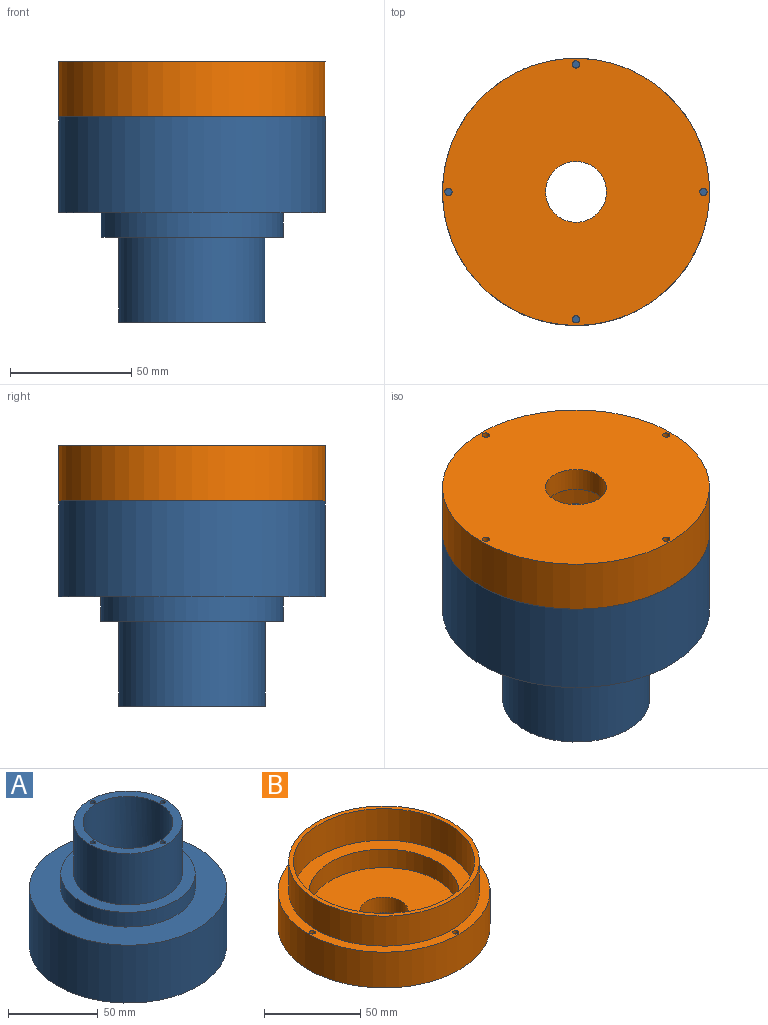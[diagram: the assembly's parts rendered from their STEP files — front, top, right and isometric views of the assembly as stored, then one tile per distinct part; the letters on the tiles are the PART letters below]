
ASSEMBLY  parts=2 mates=1
PART A: 27 faces, bbox 110x110x84.5 mm
  f0: cylinder r=25.1mm len=52.5mm, axis (0,0,-1), area 8279.7mm2, adj f2,f7
  f1: cylinder r=30.25mm len=60.5mm, axis (0,0,-1), area 6652.3mm2, adj f2,f4
  f2: plane 60.5x60.5mm, normal (0,0,1), area 867.2mm2, adj f0,f1,f19,f21,f23,f25
  f3: cylinder r=37.5mm len=75mm, axis (0,0,1), area 2356.2mm2, adj f4,f6
  f4: plane 75x75mm, normal (0,0,1), area 1543.1mm2, adj f1,f3
  f5: cylinder r=55mm len=110mm, axis (0,0,1), area 13650.2mm2, adj f6,f10
  f6: plane 110x110mm, normal (0,0,1), area 5085.5mm2, adj f3,f5
  f7: cone r=50.03mm half-angle=64.3deg, axis (0,0,-1), area 6531.6mm2, adj f0,f8
  f8: plane 100.07x100.07mm, normal (0,0,1), area 10.7mm2, adj f7,f9
  f9: cylinder r=50mm len=100mm, axis (0,0,1), area 6283.2mm2, adj f8,f10
  f10: plane 110x110mm, normal (0,0,-1), area 1615.2mm2, adj f5,f9,f11,f13,f15,f17
  f11: cylinder r=1.65mm len=25mm, axis (0,0,-1), area 259mm2, adj f10,f12
  f12: plane 3.3x3.3mm, normal (0,0,-1), area 8.5mm2, adj f11
  f13: cylinder r=1.65mm len=25mm, axis (0,0,-1), area 259mm2, adj f10,f14
  f14: plane 3.3x3.3mm, normal (0,0,-1), area 8.5mm2, adj f13
  f15: cylinder r=1.65mm len=25mm, axis (0,0,-1), area 259mm2, adj f10,f16
  f16: plane 3.3x3.3mm, normal (0,0,-1), area 8.5mm2, adj f15
  f17: cylinder r=1.65mm len=25mm, axis (0,0,-1), area 259mm2, adj f10,f18
  f18: plane 3.3x3.3mm, normal (0,0,-1), area 8.5mm2, adj f17
  f19: cylinder r=1.5mm len=20mm, axis (0,0,1), area 188.5mm2, adj f2,f20
  f20: plane 3x3mm, normal (0,0,1), area 7.1mm2, adj f19
  f21: cylinder r=1.5mm len=20mm, axis (0,0,1), area 188.5mm2, adj f2,f22
  f22: plane 3x3mm, normal (0,0,1), area 7.1mm2, adj f21
  f23: cylinder r=1.5mm len=20mm, axis (0,0,1), area 188.5mm2, adj f2,f24
  f24: plane 3x3mm, normal (0,0,1), area 7.1mm2, adj f23
  f25: cylinder r=1.5mm len=20mm, axis (0,0,1), area 188.5mm2, adj f2,f26
  f26: plane 3x3mm, normal (0,0,1), area 7.1mm2, adj f25
PART B: 14 faces, bbox 110x110x41.7 mm
  f0: plane 94x94mm, normal (0,0,1), area 2161.4mm2, adj f1,f3
  f1: cylinder r=47mm len=94mm, axis (0,0,1), area 5906.2mm2, adj f0,f5
  f2: plane 78x78mm, normal (0,0,1), area 4284.6mm2, adj f3,f9
  f3: cylinder r=39mm len=78mm, axis (0,0,1), area 2867mm2, adj f0,f2
  f4: cylinder r=49.5mm len=99mm, axis (0,0,-1), area 5909.3mm2, adj f5,f8
  f5: plane 99x99mm, normal (0,0,1), area 757.9mm2, adj f1,f4
  f6: plane 110x110mm, normal (0,0,-1), area 8981.3mm2, adj f7,f9,f10,f11,f12,f13
  f7: cylinder r=55mm len=110mm, axis (0,0,-1), area 7844.6mm2, adj f6,f8
  f8: plane 110x110mm, normal (0,0,1), area 1777.4mm2, adj f4,f7,f10,f11,f12,f13
  f9: cylinder r=12.54mm len=25.07mm, axis (0,0,1), area 787.7mm2, adj f2,f6
  f10: cylinder r=1.5mm len=22.7mm, axis (0,0,1), area 213.9mm2, adj f6,f8
  f11: cylinder r=1.5mm len=22.7mm, axis (0,0,1), area 213.9mm2, adj f6,f8
  f12: cylinder r=1.5mm len=22.7mm, axis (0,0,1), area 213.9mm2, adj f6,f8
  f13: cylinder r=1.5mm len=22.7mm, axis (0,0,1), area 213.9mm2, adj f6,f8
PLACE A rot(axis=(0,1,0),180deg) t=(157.38,105.26,14.35)mm
PLACE B rot(axis=(0,1,0),180deg) t=(157.38,105.26,86.55)mm
MATE cylindrical B.f9 <-> A.f3  axis (0,0,-1) through (157.38,105.26,63.85)mm
